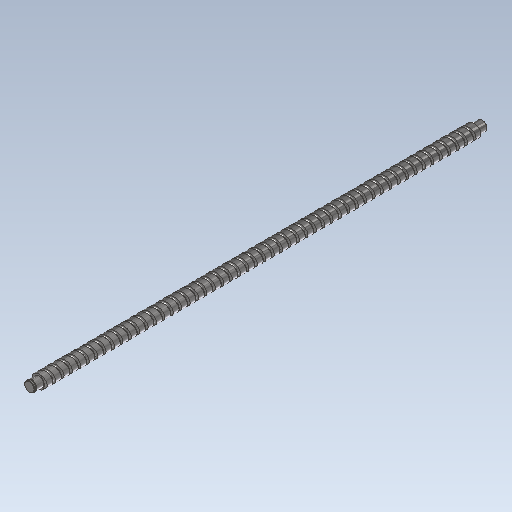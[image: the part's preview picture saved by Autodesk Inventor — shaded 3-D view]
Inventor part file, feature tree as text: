
AUTODESK INVENTOR PART (.ipt)
format: ipt  version: 2020 (Build 240168000, 168)  size: 728,576 bytes
history: native  units: mm
features: sketch x7, extrude x6, other x4, chamfer x2
ambient origin geometry x8: Origin, YZ Plane, XZ Plane, XY Plane, X Axis, Y Axis, Z Axis, Center Point
bodies: Body1 (feature_tree)
feature tree (19):
  other  "Bryła1"
  extrude  "Wyciągnięcie proste1"  Depth=12.89mm
  other  "Zwój1"
  extrude  "Wyciągnięcie proste3"  Depth=700.0mm TaperAngle=0.0deg
  extrude  "Wyciągnięcie proste4"  Depth=3.175mm
  chamfer  "Faza1"  Distance=8.0325mm
  other  "Płaszczyzna konstrukcyjna1"
  extrude  "Wyciągnięcie proste5"  Depth=3.175mm
  extrude  "Wyciągnięcie proste6"  Depth=10.0mm
  other  "Płaszczyzna konstrukcyjna2"
  extrude  "Wyciągnięcie proste7"  Depth=8.0mm
  chamfer  "Faza4"  [1 undecoded]
  sketch  "Szkic1"
  sketch  "Szkic2"
  sketch  "Szkic4"
  sketch  "Szkic5"
  sketch  "Szkic6"
  sketch  "Szkic7"
  sketch  "Szkic8"
note: 1 required parameter value undecoded (feature->parameter linkage not recoverable at this tier; creation-order binding heuristic only, values carry confidence <= 0.55)
